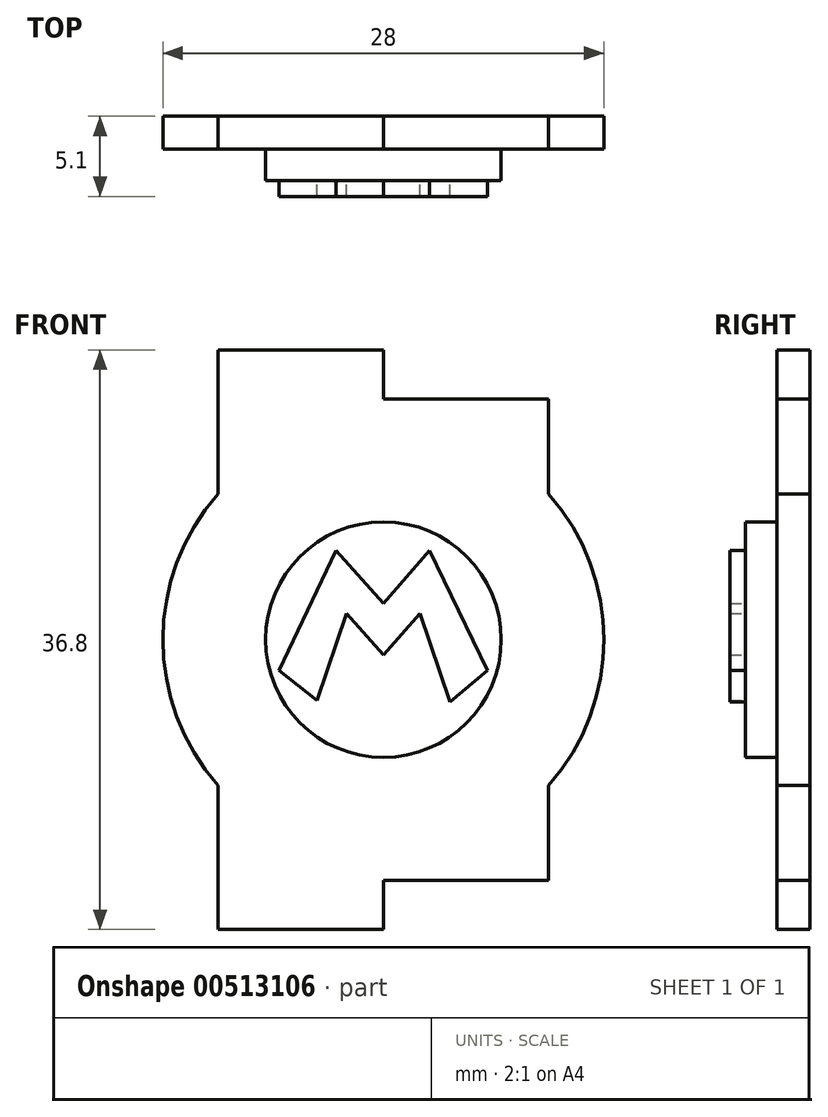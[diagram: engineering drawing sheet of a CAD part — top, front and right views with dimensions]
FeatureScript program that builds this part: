
annotation { "Feature Type Name" : "Feature", "Feature Type Description" : "" }
export const myFeature = defineFeature(function(context is Context, id is Id, definition is map)
    precondition{}
    {
        {
            var Q0;
            Q0=qCreatedBy(makeId("Front.planeOp"),FACE);
            var sketch = newSketch(context, id + "F0", { "sketchPlane" : qUnion([Q0])});
            skLineSegment(sketch, "E0", {"start": v(0, 18.4) * mm, "end": v(0, 15.3) * mm});
            skLineSegment(sketch, "E1", {"start": v(0, 15.3) * mm, "end": v(10.5, 15.3) * mm});
            skLineSegment(sketch, "E2", {"start": v(0, 18.4) * mm, "end": v(-10.5, 18.4) * mm});
            skLineSegment(sketch, "E3", {"start": v(0, -15.3) * mm, "end": v(0, -18.4) * mm});
            skLineSegment(sketch, "E4", {"start": v(0, -18.4) * mm, "end": v(-10.5, -18.4) * mm});
            skLineSegment(sketch, "E5", {"start": v(-10.5, -18.4) * mm, "end": v(-10.5, -9.26) * mm});
            skLineSegment(sketch, "E6", {"start": v(0, -15.3) * mm, "end": v(10.5, -15.3) * mm});
            skLineSegment(sketch, "E7", {"start": v(10.5, -15.3) * mm, "end": v(10.5, -9.26) * mm});
            skArc(sketch, "E8", {"start": v(-10.5, 9.26) * mm, "mid": v(-14, 0) * mm, "end": v(-10.5, -9.26) * mm});
            skArc(sketch, "E9.trimOffspring", {"start": v(10.5, -9.26) * mm, "mid": v(14, 0) * mm, "end": v(10.5, 9.26) * mm});
            skLineSegment(sketch, "E10", {"start": v(-10.5, 18.4) * mm, "end": v(-10.5, 9.26) * mm});
            skLineSegment(sketch, "E11", {"start": v(10.5, 15.3) * mm, "end": v(10.5, 9.26) * mm});
            skSolve(sketch);
        }
        {
            var Q0;
            Q0 = qSketchRegion(id + "F0", true);
            var Q1;
            Q1 = qSketchRegion(id + "F2", true);
            extrude(context, id + "F1", {"entities" : qUnion([Q0, Q1]), "depth" : 2.1 * mm, "offsetDistance" : 25 * mm});
        }
        {
            var Q0;
            Q0=makeQuery(id+"F1.opExtrude","CAP_FACE",FACE,{"disambiguationData":[OSD([sQuery(id+"F0.wireOp",EDGE,"E0"),sQuery(id+"F0.wireOp",EDGE,"E1"),sQuery(id+"F0.wireOp",EDGE,"E2"),sQuery(id+"F0.wireOp",EDGE,"E3"),sQuery(id+"F0.wireOp",EDGE,"E4"),sQuery(id+"F0.wireOp",EDGE,"E5"),sQuery(id+"F0.wireOp",EDGE,"E6"),sQuery(id+"F0.wireOp",EDGE,"E7"),sQuery(id+"F0.wireOp",EDGE,"E8"),sQuery(id+"F0.wireOp",EDGE,"E9.trimOffspring"),sQuery(id+"F0.wireOp",EDGE,"E10"),sQuery(id+"F0.wireOp",EDGE,"E11")])],"isStart":false});
            var sketch = newSketch(context, id + "F2", { "sketchPlane" : qUnion([Q0])});
            skCircle(sketch, "E12", {"center": v(0, 0) * mm, "radius": 7.48 * mm});
            skLineSegment(sketch, "E13", {"start": v(-6.62, -1.95) * mm, "end": v(-3, 5.67) * mm});
            skLineSegment(sketch, "E14", {"start": v(-3, 5.67) * mm, "end": v(0, 2.3) * mm});
            skLineSegment(sketch, "E15", {"start": v(0, 2.3) * mm, "end": v(2.94, 5.67) * mm});
            skLineSegment(sketch, "E16", {"start": v(2.94, 5.67) * mm, "end": v(6.62, -1.95) * mm});
            skLineSegment(sketch, "E17", {"start": v(6.62, -1.95) * mm, "end": v(4.23, -3.95) * mm});
            skLineSegment(sketch, "E18", {"start": v(4.23, -3.95) * mm, "end": v(2.31, 1.65) * mm});
            skLineSegment(sketch, "E19", {"start": v(2.31, 1.65) * mm, "end": v(0, -0.98) * mm});
            skLineSegment(sketch, "E20", {"start": v(0, -0.98) * mm, "end": v(-2.34, 1.68) * mm});
            skLineSegment(sketch, "E21", {"start": v(-2.34, 1.68) * mm, "end": v(-4.23, -3.87) * mm});
            skLineSegment(sketch, "E22", {"start": v(-4.23, -3.87) * mm, "end": v(-6.62, -1.95) * mm});
            skSolve(sketch);
        }
        {
            var Q0;
            Q0=makeQuery(id+"F2.imprint","IMPRINT",FACE,{"disambiguationData":[TD([[makeQuery(id+"F2.imprint","IMPRINT",EDGE,{"derivedFrom":sQuery(id+"F2.wireOp",EDGE,"E13")}),-1.0]])]});
            extrude(context, id + "F3", {"entities" : qUnion([Q0]), "operationType" : NewBodyOperationType.ADD, "depth" : 3 * mm, "offsetDistance" : 25 * mm});
        }
        {
            var Q0;
            Q0=makeQuery(id+"F2.imprint","IMPRINT",FACE,{"disambiguationData":[TD([[makeQuery(id+"F2.imprint","IMPRINT",EDGE,{"derivedFrom":sQuery(id+"F2.wireOp",EDGE,"E12")}),1.0]])]});
            extrude(context, id + "F4", {"entities" : qUnion([Q0]), "operationType" : NewBodyOperationType.ADD, "depth" : 2 * mm, "offsetDistance" : 25 * mm});
        }
    });
